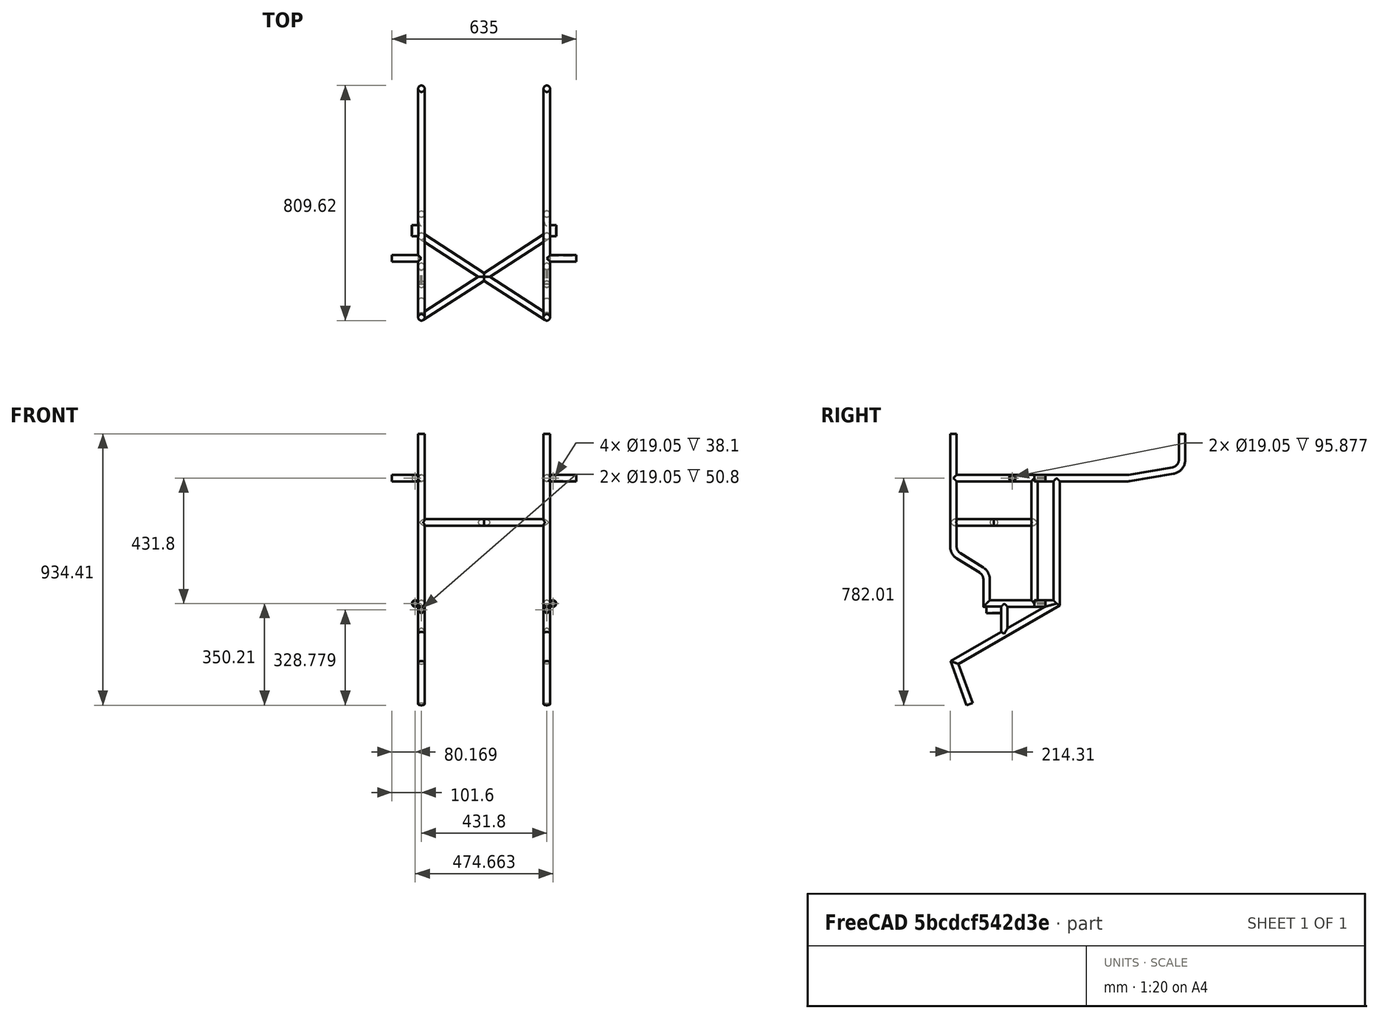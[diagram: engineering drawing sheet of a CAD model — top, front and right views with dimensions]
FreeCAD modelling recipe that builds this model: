
FCSTD DOCUMENT  (FreeCAD 0.21R33345 (Git))
Label: Frame
License: All rights reserved
LicenseURL: http://en.wikipedia.org/wiki/All_rights_reserved
objects: Sketcher::SketchObject×9, PartDesign::AdditivePipe×7, PartDesign::Plane×6, PartDesign::Pad×3, PartDesign::Mirrored×1, PartDesign::Body×1
note: 37 computed .brp shape members not serialized (recipe doc carries the construction recipe); baked Part::Feature solids carry a one-line shape summary decoded from their .brp

FEATURE [Sketcher::SketchObject] Sketch
  FullyConstrained = true
  MapMode = 5
  Placement = pos=(0,0,0) rot=(0.57735,0.57735,0.57735;2.0944rad)
  Support = -> [YZ_Plane]
  sketch-geometry (25):
    g0: LineSegment StartX=0 StartY=0 StartZ=0 EndX=0 EndY=-88.9 EndZ=0
    g1: ArcOfCircle CenterX=-38.1 CenterY=-88.9 CenterZ=0 NormalX=0 NormalY=0 NormalZ=1 AngleXU=0 Radius=38.1 StartAngle=4.87984 EndAngle=6.28319
    g2: LineSegment StartX=-31.75 StartY=-126.467 StartZ=0 EndX=-182.018 EndY=-151.867 EndZ=0
    g3: ArcOfCircle CenterX=-188.368 CenterY=-114.3 CenterZ=0 NormalX=0 NormalY=0 NormalZ=1 AngleXU=0 Radius=38.1 StartAngle=4.71239 EndAngle=4.87984
    g4: LineSegment StartX=-188.368 StartY=-152.4 StartZ=0 EndX=-431.8 EndY=-152.4 EndZ=0
    g5: LineSegment StartX=-431.8 StartY=-152.4 StartZ=0 EndX=-431.8 EndY=-584.2 EndZ=0
    g6: LineSegment StartX=-431.8 StartY=-584.2 StartZ=0 EndX=-783.753 EndY=-787.4 EndZ=0
    g7: LineSegment StartX=-783.753 StartY=-787.4 StartZ=0 EndX=-731.629 EndY=-930.609 EndZ=0
    g8: LineSegment StartX=-431.8 StartY=-152.4 StartZ=0 EndX=-508 EndY=-152.4 EndZ=0
    g9: LineSegment StartX=-508 StartY=-152.4 StartZ=0 EndX=-508 EndY=-584.2 EndZ=0
    g10: LineSegment StartX=-431.8 StartY=-584.2 StartZ=0 EndX=-508 EndY=-584.2 EndZ=0
    g11: LineSegment StartX=-508 StartY=-152.4 StartZ=0 EndX=-787.4 EndY=-152.4 EndZ=0
    g12: LineSegment StartX=-787.4 StartY=-152.4 StartZ=0 EndX=-787.4 EndY=-387.868 EndZ=0
    g13: LineSegment StartX=-673.1 StartY=-501.132 StartZ=0 EndX=-673.1 EndY=-584.2 EndZ=0
    g14: LineSegment StartX=-612.091 StartY=-584.2 StartZ=0 EndX=-612.091 EndY=-688.291 EndZ=0
    g15: LineSegment StartX=-508 StartY=-584.2 StartZ=0 EndX=-612.091 EndY=-584.2 EndZ=0
    g16: LineSegment StartX=-612.091 StartY=-584.2 StartZ=0 EndX=-673.1 EndY=-584.2 EndZ=0
    g17: ArcOfCircle CenterX=-749.3 CenterY=-387.868 CenterZ=0 NormalX=0 NormalY=0 NormalZ=1 AngleXU=0 Radius=38.1 StartAngle=3.14159 EndAngle=4.15753
    g18: LineSegment StartX=-769.372 StartY=-420.252 StartZ=0 EndX=-691.128 EndY=-468.748 EndZ=0
    g19: ArcOfCircle CenterX=-711.2 CenterY=-501.132 CenterZ=0 NormalX=0 NormalY=0 NormalZ=1 AngleXU=0 Radius=38.1 StartAngle=0 EndAngle=1.01594
    g20: LineSegment StartX=-769.372 StartY=-420.252 StartZ=0 EndX=-787.4 EndY=-387.868 EndZ=0
    g21: LineSegment StartX=-673.1 StartY=-501.132 StartZ=0 EndX=-691.128 EndY=-468.748 EndZ=0
    g22: LineSegment StartX=-778.386 StartY=-404.06 StartZ=0 EndX=-782.589 EndY=-406.4 EndZ=0
    g23: LineSegment StartX=-682.114 StartY=-484.94 StartZ=0 EndX=-677.911 EndY=-482.6 EndZ=0
    g24: LineSegment StartX=-787.4 StartY=-152.4 StartZ=0 EndX=-787.4 EndY=0 EndZ=0
  constraints (67):
    c: Coincident(g-1,g0)
    c: PointOnObject(g0,g-2)
    c: Tangent(g0,g1) = 1.5708
    c: Tangent(g2,g3) = 1.5708
    c: Horizontal(g4)
    c: Coincident(g4,g5)
    c: Vertical(g5)
    c: Coincident(g5,g6)
    c: Coincident(g6,g7)
    c: Coincident(g8,g4)
    c: Horizontal(g8)
    c: Coincident(g9,g8)
    c: Vertical(g9)
    c: Coincident(g10,g5)
    c: Coincident(g10,g9)
    c: Horizontal(g10)
    c: Coincident(g11,g8)
    c: Horizontal(g11)
    c: Coincident(g11,g12)
    c: Vertical(g12)
    c: Vertical(g13)
    c: PointOnObject(g14,g6)
    c: Vertical(g14)
    c: Tangent(g3,g4) = 1.5708
    c: Tangent(g1,g2) = 1.5708
    c: DistanceY(g0,g0) = 88.9
    c: Radius(g1) = 38.1
    c: Distance(g2) = 152.4
    c: DistanceX(g8,g8) = 76.2
    c: Angle(g10,g6) = 0.523599
    c: Angle(g7,g6) = 1.74533
    c: Distance(g7) = 152.4
    c: Distance(g6) = 406.4
    c: DistanceX(g4,g0) = 431.8
    c: DistanceY(g3,g0) = 152.4
    c: Equal(g1,g3)
    c: DistanceY(g9,g8) = 431.8
    c: DistanceX(g13,g5) = 241.3
    c: Coincident(g15,g9)
    c: Coincident(g15,g14)
    c: Horizontal(g15)
    c: Coincident(g16,g14)
    c: Coincident(g16,g13)
    c: Horizontal(g16)
    c: Equal(g15,g14)
    c: Tangent(g12,g17) = -1.5708
    c: Tangent(g19,g18) = 1.5708
    c: Tangent(g19,g13) = 1.5708
    c: Tangent(g17,g18) = -1.5708
    c: Radius(g17) = 38.1
    c: Radius(g19) = 38.1
    c: Coincident(g20,g17)
    c: Coincident(g20,g12)
    c: Coincident(g21,g13)
    c: Coincident(g21,g18)
    c: PointOnObject(g22,g20)
    c: PointOnObject(g23,g21)
    c: PointOnObject(g22,g17)
    c: PointOnObject(g23,g19)
    c: Symmetric(g18,g13,g23)
    c: Symmetric(g12,g17,g22)
    c: DistanceY(g22,g11) = 254
    c: DistanceY(g23,g22) = 76.2
    c: DistanceX(g11,g0) = 787.4
    c: Coincident(g24,g11)
    c: Vertical(g24)
    c: PointOnObject(g24,g-1)
FEATURE [Sketcher::SketchObject] Sketch001
  ExternalGeometry = -> [Sketch]
  FullyConstrained = true
  MapMode = 5
  Support = -> [XY_Plane]
  sketch-geometry (1):
    g0: Circle CenterX=0 CenterY=-787.4 CenterZ=0 NormalX=0 NormalY=0 NormalZ=1 AngleXU=0 Radius=11.1125
  constraints (2):
    c: Coincident(g0,g-3)
    c: Diameter(g0) = 22.225
FEATURE [PartDesign::AdditivePipe] AdditivePipe
  AuxilleryCurvelinear = true
  AuxillerySpineTangent = false
  Binormal = (0,0,0)
  Mode = 0
  Profile = -> Sketch001
  Refine = true
  Spine = -> Sketch [Edge16,Edge15,Edge14,Edge13,Edge12,Edge11,Edge10,Edge9]
  SpineTangent = false
  Transformation = 0
  Transition = 1
FEATURE [PartDesign::AdditivePipe] AdditivePipe001
  AuxilleryCurvelinear = true
  AuxillerySpineTangent = false
  BaseFeature = -> AdditivePipe
  Binormal = (0,0,0)
  Mode = 0
  Profile = -> Sketch001
  Refine = true
  Spine = -> Sketch [Edge16,Edge17,Edge18,Edge19]
  SpineTangent = false
  Transformation = 0
  Transition = 1
FEATURE [Sketcher::SketchObject] Sketch002
  FullyConstrained = true
  MapMode = 5
  Support = -> [XY_Plane]
  sketch-geometry (1):
    g0: Circle CenterX=0 CenterY=0 CenterZ=0 NormalX=0 NormalY=0 NormalZ=1 AngleXU=0 Radius=11.1125
  constraints (2):
    c: Coincident(g0,g-1)
    c: Diameter(g0) = 22.225
FEATURE [PartDesign::AdditivePipe] AdditivePipe002
  AuxilleryCurvelinear = true
  AuxillerySpineTangent = false
  BaseFeature = -> AdditivePipe001
  Binormal = (0,0,0)
  Mode = 0
  Profile = -> Sketch002
  Refine = true
  Spine = -> Sketch [Edge1,Edge2,Edge3,Edge4,Edge5,Edge6,Edge7,Edge8]
  SpineTangent = false
  Transformation = 0
  Transition = 1
FEATURE [PartDesign::AdditivePipe] AdditivePipe003
  AuxilleryCurvelinear = true
  AuxillerySpineTangent = false
  BaseFeature = -> AdditivePipe002
  Binormal = (0,0,0)
  Mode = 0
  Profile = -> Sketch001
  Refine = true
  Spine = -> Sketch [Edge16,Edge17,Edge21]
  SpineTangent = false
  Transformation = 0
  Transition = 1
FEATURE [PartDesign::AdditivePipe] AdditivePipe004
  AuxilleryCurvelinear = true
  AuxillerySpineTangent = false
  BaseFeature = -> AdditivePipe003
  Binormal = (0,0,0)
  Mode = 0
  Profile = -> Sketch001
  Refine = true
  Spine = -> Sketch [Edge16,Edge15,Edge14,Edge13,Edge12,Edge11,Edge10,Edge19,Edge20]
  SpineTangent = false
  Transformation = 0
  Transition = 1
FEATURE [Sketcher::SketchObject] Sketch003
  ExternalGeometry = -> [AdditivePipe004]
  FullyConstrained = true
  MapMode = 5
  Placement = pos=(0,0,0) rot=(0.57735,0.57735,0.57735;2.0944rad)
  Support = -> [YZ_Plane]
  sketch-geometry (3):
    g0: LineSegment StartX=-508 StartY=-152.4 StartZ=0 EndX=-787.4 EndY=-152.4 EndZ=0
    g1: Circle CenterX=-584.2 CenterY=-152.4 CenterZ=0 NormalX=0 NormalY=0 NormalZ=1 AngleXU=0 Radius=11.1125
    g2: Circle CenterX=-584.2 CenterY=-152.4 CenterZ=0 NormalX=0 NormalY=0 NormalZ=1 AngleXU=0 Radius=9.525
  constraints (7):
    c: Coincident(g0,g-3)
    c: Coincident(g0,g-4)
    c: PointOnObject(g1,g0)
    c: Coincident(g2,g1)
    c: Diameter(g2) = 19.05
    c: Diameter(g1) = 22.225
    c: DistanceX(g0,g1) = 203.2
FEATURE [PartDesign::Pad] Pad
  BaseFeature = -> AdditivePipe004
  Direction = (1,-2e-16,3e-16)
  Length = 101.6
  Length2 = 10
  Profile = -> Sketch003
  ReferenceAxis = -> Sketch003 [N_Axis]
  Refine = true
  Reversed = true
  Type = 0
FEATURE [PartDesign::Plane] DatumPlane
  AttachmentOffset = pos=(0,0,215.9) rot=(0,0,1;0rad)
  Length = 1001.19
  MapMode = 5
  Placement = pos=(215.9,-4.79e-14,4.79e-14) rot=(0.57735,0.57735,0.57735;2.0944rad)
  ResizeMode = 0
  Support = -> [YZ_Plane]
  Width = 1137.14
FEATURE [PartDesign::Plane] DatumPlane001
  AttachmentOffset = pos=(0,0,-304.8) rot=(0,0,1;0rad)
  Length = 779.621
  MapMode = 5
  Placement = pos=(0,0,-304.8) rot=(0,0,1;0rad)
  ResizeMode = 0
  Support = -> [XY_Plane]
  Width = 968.052
FEATURE [Sketcher::SketchObject] Sketch004
  ExternalGeometry = -> [Pad]
  FullyConstrained = true
  MapMode = 5
  Placement = pos=(0,0,-304.8) rot=(0,0,1;0rad)
  Support = -> [DatumPlane001]
  sketch-geometry (2):
    g0: LineSegment StartX=0 StartY=-508 StartZ=0 EndX=431.8 EndY=-787.4 EndZ=0
    g1: LineSegment StartX=0 StartY=-787.4 StartZ=0 EndX=431.8 EndY=-508 EndZ=0
  constraints (7):
    c: PointOnObject(g0,g-2)
    c: Horizontal(g-4,g0)
    c: DistanceY(g-4,g0) = 279.4
    c: Coincident(g1,g-4)
    c: Vertical(g1,g0)
    c: Horizontal(g0,g1)
    c: DistanceX(g0,g1) = 431.8
FEATURE [PartDesign::Plane] DatumPlane002
  AttachmentOffset = pos=(0,0,-514.31) rot=(0,0,1;0rad)
  Length = 1235.71
  MapMode = 7
  Placement = pos=(431.799,-787.4,-304.8) rot=(-0.359036,0.65996,0.65996;3.831rad)
  ResizeMode = 0
  Support = -> [Sketch004]
  Width = 1158.8
FEATURE [PartDesign::Plane] DatumPlane003
  AttachmentOffset = pos=(0,0,-514.31) rot=(0,0,1;0rad)
  Length = 1235.71
  MapMode = 7
  Placement = pos=(431.799,-508,-304.8) rot=(0.792571,-0.43118,-0.43118;1.8012rad)
  ResizeMode = 0
  Support = -> [Sketch004]
  Width = 1158.8
FEATURE [Sketcher::SketchObject] Sketch005
  FullyConstrained = true
  MapMode = 5
  Placement = pos=(431.799,-508,-304.8) rot=(0.792571,-0.43118,-0.43118;1.8012rad)
  Support = -> [DatumPlane003]
  sketch-geometry (1):
    g0: Circle CenterX=0 CenterY=0 CenterZ=0 NormalX=0 NormalY=0 NormalZ=1 AngleXU=0 Radius=11.1125
  constraints (2):
    c: Coincident(g0,g-1)
    c: Diameter(g0) = 22.225
FEATURE [Sketcher::SketchObject] Sketch006
  FullyConstrained = true
  MapMode = 5
  Placement = pos=(431.799,-787.4,-304.8) rot=(-0.359036,0.65996,0.65996;3.831rad)
  Support = -> [DatumPlane002]
  sketch-geometry (1):
    g0: Circle CenterX=0 CenterY=0 CenterZ=0 NormalX=0 NormalY=0 NormalZ=1 AngleXU=0 Radius=11.1125
  constraints (2):
    c: Coincident(g0,g-1)
    c: Diameter(g0) = 22.225
FEATURE [PartDesign::AdditivePipe] AdditivePipe005
  AuxilleryCurvelinear = true
  AuxillerySpineTangent = false
  BaseFeature = -> Pad
  Binormal = (0,0,0)
  Mode = 0
  Profile = -> Sketch006
  Refine = true
  Spine = -> Sketch004 [Edge1]
  SpineTangent = false
  Transformation = 0
  Transition = 0
FEATURE [PartDesign::AdditivePipe] AdditivePipe006
  AuxilleryCurvelinear = true
  AuxillerySpineTangent = false
  BaseFeature = -> AdditivePipe005
  Binormal = (0,0,0)
  Mode = 0
  Profile = -> Sketch005
  Refine = true
  Spine = -> Sketch004 [Edge2]
  SpineTangent = false
  Transformation = 0
  Transition = 0
FEATURE [PartDesign::Plane] DatumPlane004
  AttachmentOffset = pos=(0,0,-61.01) rot=(0,0,1;0rad)
  Length = 791.104
  MapMode = 7
  Placement = pos=(-1.97e-14,-673.101,-584.2) rot=(0,0.707107,0.707107;3.14159rad)
  ResizeMode = 0
  Support = -> [Sketch]
  Width = 1115.49
FEATURE [Sketcher::SketchObject] Sketch007
  FullyConstrained = true
  MapMode = 5
  Placement = pos=(-1.97e-14,-673.101,-584.2) rot=(0,0.707107,0.707107;3.14159rad)
  Support = -> [DatumPlane004]
  sketch-geometry (7):
    g0: Circle CenterX=0 CenterY=0 CenterZ=0 NormalX=0 NormalY=0 NormalZ=1 AngleXU=0 Radius=11.1125
    g1: Circle CenterX=0 CenterY=-21.4312 CenterZ=0 NormalX=0 NormalY=0 NormalZ=1 AngleXU=0 Radius=9.525
    g2: Circle CenterX=0 CenterY=-21.4312 CenterZ=0 NormalX=0 NormalY=0 NormalZ=1 AngleXU=0 Radius=11.1125
    g3: Circle CenterX=0 CenterY=-21.4312 CenterZ=0 NormalX=0 NormalY=0 NormalZ=1 AngleXU=0 Radius=10.3188
    g4: LineSegment StartX=0 StartY=-21.4312 StartZ=0 EndX=-11.1125 EndY=-21.4312 EndZ=0
    g5: GeomPoint X=-9.525 Y=-21.4312 Z=0
    g6: GeomPoint X=-10.3188 Y=-21.4312 Z=0
  constraints (15):
    c: Coincident(g0,g-1)
    c: Diameter(g0) = 22.225
    c: PointOnObject(g1,g-2)
    c: Coincident(g2,g1)
    c: Diameter(g2) = 22.225
    c: Diameter(g1) = 19.05
    c: Coincident(g3,g1)
    c: Coincident(g4,g1)
    c: PointOnObject(g4,g2)
    c: Horizontal(g4)
    c: PointOnObject(g5,g4)
    c: PointOnObject(g5,g1)
    c: PointOnObject(g6,g3)
    c: Symmetric(g4,g5,g6)
    c: Tangent(g0,g3)
FEATURE [PartDesign::Pad] Pad001
  BaseFeature = -> AdditivePipe006
  Direction = (2e-16,1,-2e-16)
  Length = 50.8
  Length2 = 10
  Profile = -> Sketch007
  ReferenceAxis = -> Sketch007 [N_Axis]
  Refine = true
  Type = 0
FEATURE [PartDesign::Plane] DatumPlane005
  AttachmentOffset = pos=(0,0,0) rot=(1,0,0;1.5708rad)
  Length = 791.104
  MapMode = 7
  Placement = pos=(-7.9e-14,-508,-152.4) rot=(1,0,0;1.5708rad)
  ResizeMode = 0
  Support = -> [Sketch]
  Width = 1115.49
FEATURE [PartDesign::Mirrored] Mirrored
  BaseFeature = -> Pad001
  MirrorPlane = -> DatumPlane
  Originals = -> [AdditivePipe,AdditivePipe001,AdditivePipe002,AdditivePipe003,AdditivePipe004,Pad,AdditivePipe005,AdditivePipe006,Pad001]
  Refine = true
FEATURE [Sketcher::SketchObject] Sketch008
  ExternalGeometry = -> [Mirrored]
  FullyConstrained = false
  MapMode = 5
  Placement = pos=(-7.9e-14,-508,-152.4) rot=(1,0,0;1.5708rad)
  Support = -> [DatumPlane005]
  sketch-geometry (14):
    g0: Circle CenterX=431.8 CenterY=0.532893 CenterZ=0 NormalX=0 NormalY=0 NormalZ=1 AngleXU=0 Radius=11.1125
    g1: Circle CenterX=453.225 CenterY=0 CenterZ=0 NormalX=0 NormalY=0 NormalZ=1 AngleXU=0 Radius=11.1125
    g2: Circle CenterX=453.225 CenterY=0 CenterZ=0 NormalX=0 NormalY=0 NormalZ=1 AngleXU=0 Radius=9.525
    g3: LineSegment StartX=-11.1113 StartY=-267.99 StartZ=0 EndX=-11.1113 EndY=100 EndZ=0
    g4: Circle CenterX=453.231 CenterY=-431.8 CenterZ=0 NormalX=0 NormalY=0 NormalZ=1 AngleXU=0 Radius=9.525
    g5: Circle CenterX=453.231 CenterY=-431.8 CenterZ=0 NormalX=0 NormalY=0 NormalZ=1 AngleXU=0 Radius=11.1125
    g6: Circle CenterX=453.225 CenterY=0 CenterZ=0 NormalX=0 NormalY=0 NormalZ=1 AngleXU=0 Radius=10.3187
    g7: LineSegment StartX=453.225 StartY=0 StartZ=0 EndX=464.337 EndY=0 EndZ=0
    g8: GeomPoint X=462.75 Y=0 Z=0
    g9: GeomPoint X=463.543 Y=0 Z=0
    g10: Circle CenterX=-21.4246 CenterY=0 CenterZ=0 NormalX=0 NormalY=0 NormalZ=1 AngleXU=0 Radius=11.1125
    g11: Circle CenterX=-21.4246 CenterY=0 CenterZ=0 NormalX=0 NormalY=0 NormalZ=1 AngleXU=0 Radius=9.525
    g12: Circle CenterX=-21.4313 CenterY=-431.8 CenterZ=0 NormalX=0 NormalY=0 NormalZ=1 AngleXU=0 Radius=9.525
    g13: Circle CenterX=-21.4313 CenterY=-431.8 CenterZ=0 NormalX=0 NormalY=0 NormalZ=1 AngleXU=0 Radius=11.1125
  constraints (25):
    c: Diameter(g0) = 22.225
    c: PointOnObject(g1,g-1)
    c: Coincident(g2,g1)
    c: Diameter(g1) = 22.225
    c: Diameter(g2) = 19.05
    c: PointOnObject(g3,g-4)
    c: Vertical(g3)
    c: Coincident(g4,g5)
    c: Diameter(g5) = 22.225
    c: Diameter(g4) = 19.05
    c: Coincident(g6,g1)
    c: Coincident(g7,g1)
    c: PointOnObject(g7,g1)
    c: Horizontal(g7)
    c: PointOnObject(g8,g2)
    c: PointOnObject(g8,g7)
    c: PointOnObject(g9,g6)
    c: Symmetric(g8,g7,g9)
    c: Tangent(g6,g0)
    c: Coincident(g11,g10)
    c: Diameter(g10) = 22.225
    c: Diameter(g11) = 19.05
    c: Coincident(g12,g13)
    c: Diameter(g13) = 22.225
    c: Diameter(g12) = 19.05
FEATURE [PartDesign::Pad] Pad002
  BaseFeature = -> Mirrored
  Direction = (0,-1,2e-16)
  Length = 38.1
  Length2 = 10
  Profile = -> Sketch008
  ReferenceAxis = -> Sketch008 [N_Axis]
  Refine = true
  Reversed = true
  Type = 0
FEATURE [PartDesign::Body] Body
  Group = -> [Sketch,Sketch001,AdditivePipe,AdditivePipe001,Sketch002,AdditivePipe002,AdditivePipe003,AdditivePipe004,Sketch003,Pad,DatumPlane,DatumPlane001,Sketch004,DatumPlane002,DatumPlane003,Sketch005,Sketch006,AdditivePipe005,AdditivePipe006,DatumPlane004,Sketch007,Pad001,DatumPlane005,Mirrored,Sketch008,Pad002]
  Origin = -> Origin
  Tip = -> Pad002
